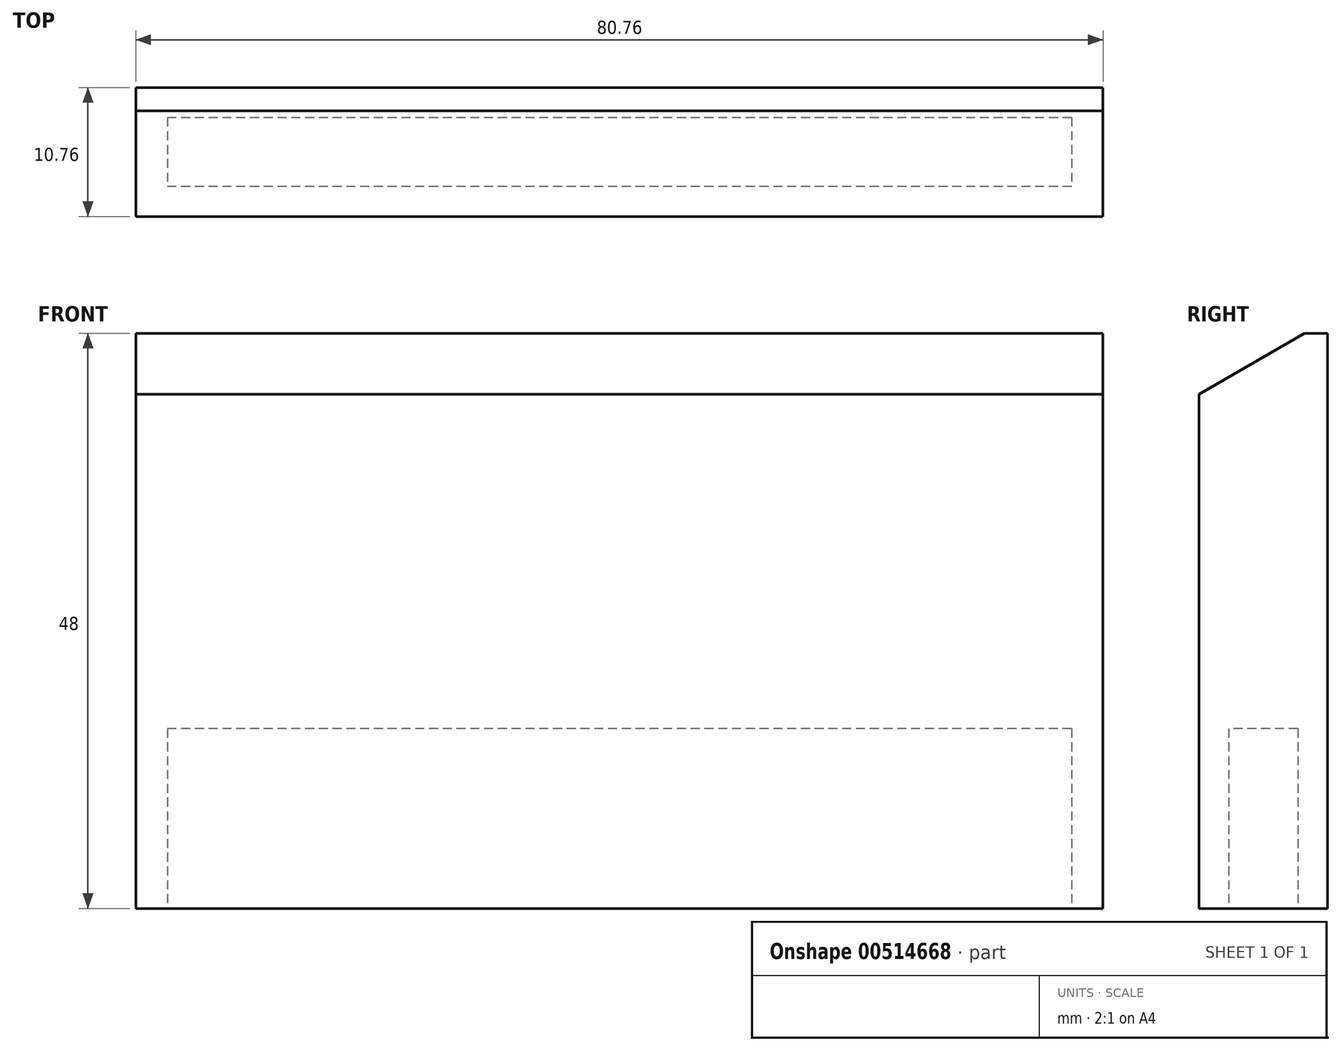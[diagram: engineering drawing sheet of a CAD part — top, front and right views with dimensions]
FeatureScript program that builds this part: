
annotation { "Feature Type Name" : "Feature", "Feature Type Description" : "" }
export const myFeature = defineFeature(function(context is Context, id is Id, definition is map)
    precondition{}
    {
        {
            var Q0;
            Q0=qCreatedBy(makeId("Top.planeOp"),FACE);
            var sketch = newSketch(context, id + "F0", { "sketchPlane" : qUnion([Q0])});
            skLineSegment(sketch, "E0.bottom", {"start": v(40.38, -5.38) * mm, "end": v(-40.38, -5.38) * mm});
            skLineSegment(sketch, "E0.top", {"start": v(40.38, 5.38) * mm, "end": v(-40.38, 5.37) * mm});
            skLineSegment(sketch, "E0.left", {"start": v(40.38, -5.38) * mm, "end": v(40.38, 5.38) * mm});
            skLineSegment(sketch, "E0.right", {"start": v(-40.38, -5.38) * mm, "end": v(-40.38, 5.37) * mm});
            skPoint(sketch, "E0.middle", {"position": v(0, 0) * mm});
            skSolve(sketch);
        }
        {
            var Q0;
            Q0=makeQuery(id+"F0.imprint","IMPRINT",FACE,{"disambiguationData":[TD([[makeQuery(id+"F0.imprint","IMPRINT",EDGE,{"derivedFrom":sQuery(id+"F0.wireOp",EDGE,"E0.bottom")}),-1.0]])]});
            extrude(context, id + "F1", {"entities" : qUnion([Q0]), "depth" : 48 * mm, "offsetDistance" : 25.4 * mm});
        }
        {
            var Q0;
            Q0=makeQuery(id+"F1.opExtrude","CAP_FACE",FACE,{"disambiguationData":[OSD([sQuery(id+"F0.wireOp",EDGE,"E0.bottom"),sQuery(id+"F0.wireOp",EDGE,"E0.top"),sQuery(id+"F0.wireOp",EDGE,"E0.left"),sQuery(id+"F0.wireOp",EDGE,"E0.right")])],"isStart":true});
            var sketch = newSketch(context, id + "F2", { "sketchPlane" : qUnion([Q0])});
            skLineSegment(sketch, "E1.bottom", {"start": v(37.75, -2.87) * mm, "end": v(-37.75, -2.87) * mm});
            skLineSegment(sketch, "E1.top", {"start": v(37.75, 2.88) * mm, "end": v(-37.75, 2.88) * mm});
            skLineSegment(sketch, "E1.left", {"start": v(37.75, -2.87) * mm, "end": v(37.75, 2.88) * mm});
            skLineSegment(sketch, "E1.right", {"start": v(-37.75, -2.87) * mm, "end": v(-37.75, 2.88) * mm});
            skPoint(sketch, "E1.middle", {"position": v(0, 0) * mm});
            skSolve(sketch);
        }
        {
            var Q0;
            Q0=makeQuery(id+"F2.imprint","IMPRINT",FACE,{"disambiguationData":[TD([[makeQuery(id+"F2.imprint","IMPRINT",EDGE,{"derivedFrom":sQuery(id+"F2.wireOp",EDGE,"E1.bottom")}),-1.0]])]});
            extrude(context, id + "F3", {"entities" : qUnion([Q0]), "operationType" : NewBodyOperationType.REMOVE, "oppositeDirection" : true, "depth" : 15 * mm, "offsetDistance" : 25.4 * mm});
        }
        {
            var Q0;
            Q0=makeQuery(id+"F1.opExtrude","CAP_EDGE",EDGE,{"disambiguationData":[OSD([sQuery(id+"F0.wireOp",EDGE,"E0.bottom")])],"isStart":false});
            chamfer(context, id + "F4", {"entities" : qUnion([Q0]), "chamferType" : ChamferType.OFFSET_ANGLE, "width" : 5.08 * mm, "oppositeDirection" : false, "angle" : 60 * degree, "tangentPropagation" : true});
        }
    });
